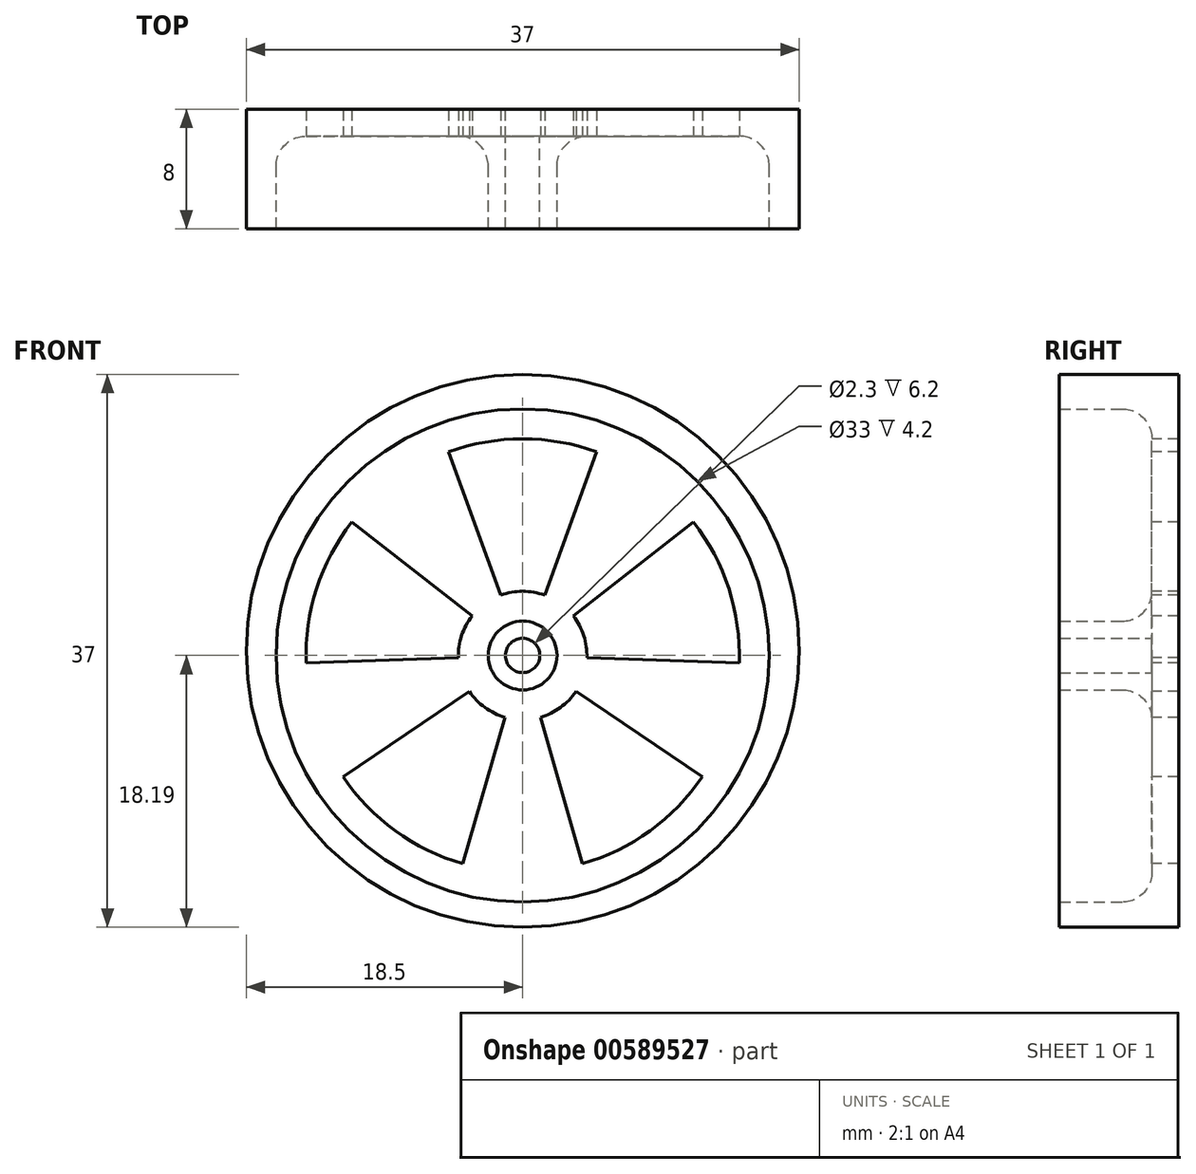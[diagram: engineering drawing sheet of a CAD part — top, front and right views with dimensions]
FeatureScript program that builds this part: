
annotation { "Feature Type Name" : "Feature", "Feature Type Description" : "" }
export const myFeature = defineFeature(function(context is Context, id is Id, definition is map)
    precondition{}
    {
        {
            var Q0;
            Q0=qCreatedBy(makeId("Front.planeOp"),FACE);
            var sketch = newSketch(context, id + "F0", { "sketchPlane" : qUnion([Q0])});
            skCircle(sketch, "E0", {"center": v(0, 0) * mm, "radius": 1.15 * mm});
            skCircle(sketch, "E1", {"center": v(0, 0) * mm, "radius": 2.3 * mm});
            skCircle(sketch, "E2", {"center": v(0, 0.31) * mm, "radius": 18.5 * mm});
            skCircle(sketch, "E3", {"center": v(0, 0) * mm, "radius": 16.5 * mm});
            skSolve(sketch);
        }
        {
            var Q0;
            Q0=makeQuery(id+"F0.imprint","IMPRINT",FACE,{"disambiguationData":[TD([[makeQuery(id+"F0.imprint","IMPRINT",EDGE,{"derivedFrom":sQuery(id+"F0.wireOp",EDGE,"E0")}),-1.0]])]});
            extrude(context, id + "F1", {"entities" : qUnion([Q0]), "depth" : 8 * mm, "offsetDistance" : 25 * mm});
        }
        {
            var Q0;
            Q0=makeQuery(id+"F0.imprint","IMPRINT",FACE,{"disambiguationData":[TD([[makeQuery(id+"F0.imprint","IMPRINT",EDGE,{"derivedFrom":sQuery(id+"F0.wireOp",EDGE,"E2")}),1.0]])]});
            extrude(context, id + "F2", {"entities" : qUnion([Q0]), "depth" : 8 * mm, "offsetDistance" : 25 * mm});
        }
        {
            var Q0;
            Q0=makeQuery(id+"F0.imprint","IMPRINT",FACE,{"disambiguationData":[TD([[makeQuery(id+"F0.imprint","IMPRINT",EDGE,{"derivedFrom":sQuery(id+"F0.wireOp",EDGE,"E2")}),1.0]])]});
            var Q1;
            Q1=makeQuery(id+"F0.imprint","IMPRINT",FACE,{"disambiguationData":[TD([[makeQuery(id+"F0.imprint","IMPRINT",EDGE,{"derivedFrom":sQuery(id+"F0.wireOp",EDGE,"E1")}),-1.0]])]});
            var Q2;
            Q2=makeQuery(id+"F0.imprint","IMPRINT",FACE,{"disambiguationData":[TD([[makeQuery(id+"F0.imprint","IMPRINT",EDGE,{"derivedFrom":sQuery(id+"F0.wireOp",EDGE,"E0")}),1.0]])]});
            var Q3;
            Q3=makeQuery(id+"F0.imprint","IMPRINT",FACE,{"disambiguationData":[TD([[makeQuery(id+"F0.imprint","IMPRINT",EDGE,{"derivedFrom":sQuery(id+"F0.wireOp",EDGE,"E0")}),-1.0]])]});
            extrude(context, id + "F3", {"entities" : qUnion([Q0, Q1, Q2, Q3]), "operationType" : NewBodyOperationType.ADD, "depth" : 1.8 * mm, "offsetDistance" : 25 * mm});
        }
        {
            var Q0;
            Q0=makeQuery(id+"F3.boolean.opBoolean","INTERSECT",EDGE,{"derivedFrom":[makeQuery(id+"F2.opExtrude","SWEPT_FACE",FACE,{"disambiguationData":[OSD([sQuery(id+"F0.wireOp",EDGE,"E3")])]}),makeQuery(id+"F3.opExtrude","CAP_FACE",FACE,{"disambiguationData":[OSD([sQuery(id+"F0.wireOp",EDGE,"E2")])],"isStart":false})]});
            var Q1;
            Q1=makeQuery(id+"F3.boolean.opBoolean","INTERSECT",EDGE,{"derivedFrom":[makeQuery(id+"F1.opExtrude","SWEPT_FACE",FACE,{"disambiguationData":[OSD([sQuery(id+"F0.wireOp",EDGE,"E1")])]}),makeQuery(id+"F3.opExtrude","CAP_FACE",FACE,{"disambiguationData":[OSD([sQuery(id+"F0.wireOp",EDGE,"E2")])],"isStart":false})]});
            fillet(context, id + "F4", {"entities" : qUnion([Q0, Q1]), "radius" : 2 * mm, "tangentPropagation" : true, "allowEdgeOverflow" : false});
        }
        {
            var Q0;
            Q0=makeQuery(id+"F3.boolean.opBoolean","SPLIT",FACE,{"disambiguationData":[TD([makeQuery(id+"F1.opExtrude","SWEPT_FACE",FACE,{"disambiguationData":[OSD([sQuery(id+"F0.wireOp",EDGE,"E1")])]})])],"derivedFrom":makeQuery(id+"F3.opExtrude","CAP_FACE",FACE,{"disambiguationData":[OSD([sQuery(id+"F0.wireOp",EDGE,"E2")])],"isStart":false})});
            var sketch = newSketch(context, id + "F5", { "sketchPlane" : qUnion([Q0])});
            skCircle(sketch, "E4.0", {"center": v(0, 0) * mm, "radius": 14.5 * mm});
            skCircle(sketch, "E4.1", {"center": v(0, 0) * mm, "radius": 4.3 * mm});
            skLineSegment(sketch, "E5", {"start": v(-1.47, 4.04) * mm, "end": v(-4.96, 13.63) * mm});
            skLineSegment(sketch, "E6", {"start": v(1.47, 4.04) * mm, "end": v(4.96, 13.63) * mm});
            skLineSegment(sketch, "E7.1.0", {"start": v(-4.3, -0.15) * mm, "end": v(-14.5, -0.5) * mm});
            skLineSegment(sketch, "E7.1.2", {"start": v(-3.39, 2.65) * mm, "end": v(-11.43, 8.93) * mm});
            skLineSegment(sketch, "E7.2.0", {"start": v(-1.19, -4.13) * mm, "end": v(-4, -13.94) * mm});
            skLineSegment(sketch, "E7.2.2", {"start": v(-3.56, -2.4) * mm, "end": v(-12.02, -8.1) * mm});
            skLineSegment(sketch, "E7.3.0", {"start": v(3.56, -2.4) * mm, "end": v(12.02, -8.1) * mm});
            skLineSegment(sketch, "E7.3.2", {"start": v(1.19, -4.13) * mm, "end": v(4, -13.94) * mm});
            skLineSegment(sketch, "E7.4.0", {"start": v(3.39, 2.65) * mm, "end": v(11.43, 8.93) * mm});
            skLineSegment(sketch, "E7.4.2", {"start": v(4.3, -0.15) * mm, "end": v(14.5, -0.5) * mm});
            skSolve(sketch);
        }
        {
            var Q0;
            {var subQ0=sQuery(id+"F5.wireOp",EDGE,"E5");Q0=makeQuery(id+"F5.imprint","IMPRINT",FACE,{"disambiguationData":[TD([[makeQuery(id+"F5.imprint","IMPRINT",EDGE,{"derivedFrom":subQ0}),-1.0]])]});}
            var Q1;
            {var subQ0=sQuery(id+"F5.wireOp",EDGE,"E7.4.0");Q1=makeQuery(id+"F5.imprint","IMPRINT",FACE,{"disambiguationData":[TD([[makeQuery(id+"F5.imprint","IMPRINT",EDGE,{"derivedFrom":subQ0}),-1.0]])]});}
            var Q2;
            {var subQ0=sQuery(id+"F5.wireOp",EDGE,"E7.3.0");Q2=makeQuery(id+"F5.imprint","IMPRINT",FACE,{"disambiguationData":[TD([[makeQuery(id+"F5.imprint","IMPRINT",EDGE,{"derivedFrom":subQ0}),-1.0]])]});}
            var Q3;
            {var subQ0=sQuery(id+"F5.wireOp",EDGE,"E7.2.0");Q3=makeQuery(id+"F5.imprint","IMPRINT",FACE,{"disambiguationData":[TD([[makeQuery(id+"F5.imprint","IMPRINT",EDGE,{"derivedFrom":subQ0}),-1.0]])]});}
            var Q4;
            {var subQ0=sQuery(id+"F5.wireOp",EDGE,"E7.1.0");Q4=makeQuery(id+"F5.imprint","IMPRINT",FACE,{"disambiguationData":[TD([[makeQuery(id+"F5.imprint","IMPRINT",EDGE,{"derivedFrom":subQ0}),-1.0]])]});}
            extrude(context, id + "F6", {"entities" : qUnion([Q0, Q1, Q2, Q3, Q4]), "operationType" : NewBodyOperationType.REMOVE, "endBound" : BoundingType.THROUGH_ALL, "oppositeDirection" : true, "depth" : 25 * mm, "offsetDistance" : 25 * mm});
        }
    });
